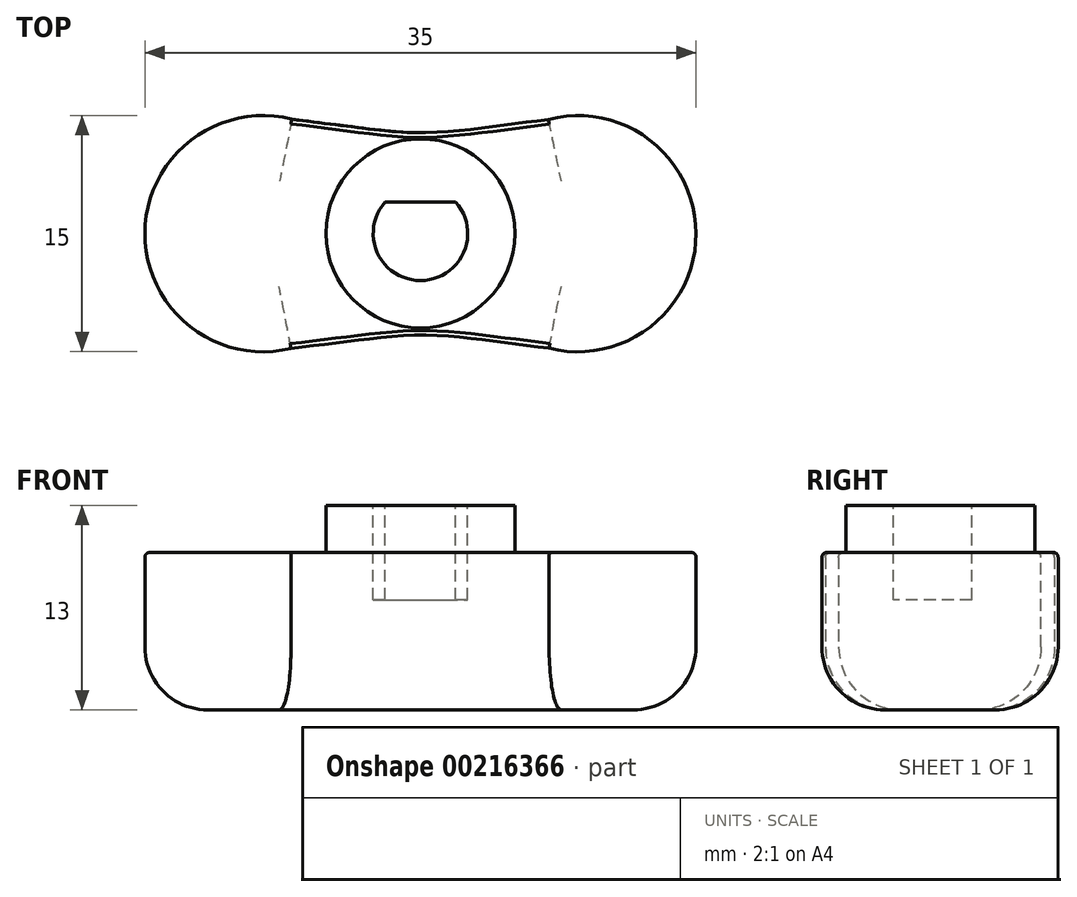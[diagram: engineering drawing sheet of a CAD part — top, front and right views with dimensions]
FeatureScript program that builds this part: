
annotation { "Feature Type Name" : "Feature", "Feature Type Description" : "" }
export const myFeature = defineFeature(function(context is Context, id is Id, definition is map)
    precondition{}
    {
        {
            var Q0;
            Q0=qCreatedBy(makeId("Top.planeOp"),FACE);
            var sketch = newSketch(context, id + "F0", { "sketchPlane" : qUnion([Q0])});
            skCircle(sketch, "E0", {"center": v(-62.73, 39.28) * mm, "radius": 7.5 * mm});
            skCircle(sketch, "E1", {"center": v(-42.73, 39.28) * mm, "radius": 7.5 * mm});
            skFitSpline(sketch, "E2", {"points": [v(-62.73, 46.78) * mm, v(-42.73, 46.78) * mm], "startDerivative": vector(35.58, -4.34) * mm, "endDerivative": vector(34.63, 4.34) * mm});
            skFitSpline(sketch, "E3", {"points": [v(-62.73, 31.78) * mm, v(-42.73, 31.78) * mm], "startDerivative": vector(35.58, 4.23) * mm, "endDerivative": vector(34.63, -4.23) * mm});
            skSolve(sketch);
        }
        {
            var Q0;
            Q0 = qSketchRegion(id + "F0", true);
            extrude(context, id + "F1", {"entities" : qUnion([Q0]), "depth" : 10 * mm, "offsetDistance" : 25 * mm});
        }
        {
            var Q0;
            Q0=makeQuery(id+"F1.opExtrude","CAP_FACE",FACE,{"disambiguationData":[OSD([sQuery(id+"F0.wireOp",EDGE,"E0"),sQuery(id+"F0.wireOp",EDGE,"E1"),sQuery(id+"F0.wireOp",EDGE,"E2"),sQuery(id+"F0.wireOp",EDGE,"E3")])],"isStart":false});
            var sketch = newSketch(context, id + "F2", { "sketchPlane" : qUnion([Q0])});
            skCircle(sketch, "E4", {"center": v(-52.73, 39.3) * mm, "radius": 6 * mm});
            skPoint(sketch, "E4.centerSnap0", {"position": v(-70.23, 39.3) * mm});
            skSolve(sketch);
        }
        {
            var Q0;
            Q0=makeQuery(id+"F2.imprint","IMPRINT",FACE,{"disambiguationData":[TD([[makeQuery(id+"F2.imprint","IMPRINT",EDGE,{"derivedFrom":sQuery(id+"F2.wireOp",EDGE,"E4")}),1.0]])]});
            extrude(context, id + "F3", {"entities" : qUnion([Q0]), "operationType" : NewBodyOperationType.ADD, "depth" : 3 * mm, "offsetDistance" : 25 * mm});
        }
        {
            var Q0;
            Q0=makeQuery(id+"F3.opExtrude","CAP_FACE",FACE,{"disambiguationData":[OSD([sQuery(id+"F2.wireOp",EDGE,"E4")])],"isStart":false});
            var sketch = newSketch(context, id + "F4", { "sketchPlane" : qUnion([Q0])});
            skCircle(sketch, "E5", {"center": v(-52.73, 39.3) * mm, "radius": 3 * mm});
            skLineSegment(sketch, "E6", {"start": v(-54.97, 41.3) * mm, "end": v(-50.5, 41.3) * mm});
            skSolve(sketch);
        }
        {
            var Q0;
            {var subQ0=sQuery(id+"F4.wireOp",EDGE,"E6");Q0=makeQuery(id+"F4.imprint","IMPRINT",FACE,{"disambiguationData":[TD([[makeQuery(id+"F4.imprint","IMPRINT",EDGE,{"derivedFrom":subQ0}),-1.0]])]});}
            extrude(context, id + "F5", {"entities" : qUnion([Q0]), "operationType" : NewBodyOperationType.REMOVE, "oppositeDirection" : true, "depth" : 6 * mm, "offsetDistance" : 25 * mm});
        }
        {
            var Q0;
            Q0=makeQuery(id+"F1.opExtrude","CAP_EDGE",EDGE,{"disambiguationData":[OSD([sQuery(id+"F0.wireOp",EDGE,"E0")])],"isStart":false});
            var Q1;
            Q1=makeQuery(id+"F1.opExtrude","CAP_EDGE",EDGE,{"disambiguationData":[OSD([sQuery(id+"F0.wireOp",EDGE,"E2")])],"isStart":false});
            var Q2;
            Q2=makeQuery(id+"F1.opExtrude","CAP_EDGE",EDGE,{"disambiguationData":[OSD([sQuery(id+"F0.wireOp",EDGE,"E1")])],"isStart":false});
            var Q3;
            Q3=makeQuery(id+"F1.opExtrude","CAP_EDGE",EDGE,{"disambiguationData":[OSD([sQuery(id+"F0.wireOp",EDGE,"E3")])],"isStart":false});
            fillet(context, id + "F6", {"entities" : qUnion([Q0, Q1, Q2, Q3]), "radius" : 0.3 * mm, "tangentPropagation" : true, "allowEdgeOverflow" : false});
        }
        {
            var Q0;
            Q0=makeQuery(id+"F1.opExtrude","CAP_FACE",FACE,{"disambiguationData":[OSD([sQuery(id+"F0.wireOp",EDGE,"E0"),sQuery(id+"F0.wireOp",EDGE,"E1"),sQuery(id+"F0.wireOp",EDGE,"E2"),sQuery(id+"F0.wireOp",EDGE,"E3")])],"isStart":true});
            fillet(context, id + "F7", {"entities" : qUnion([Q0]), "radius" : 4 * mm, "tangentPropagation" : true, "allowEdgeOverflow" : false});
        }
    });
